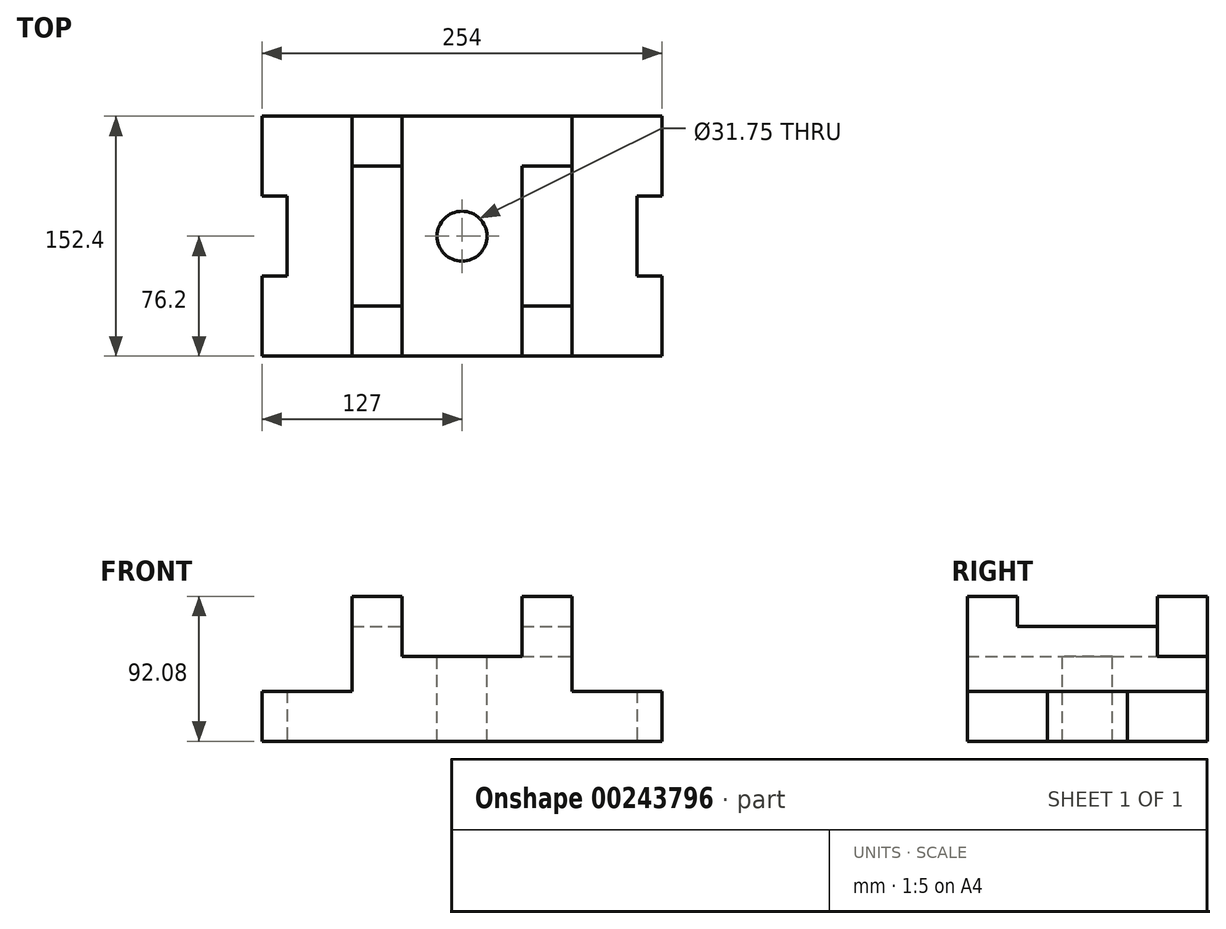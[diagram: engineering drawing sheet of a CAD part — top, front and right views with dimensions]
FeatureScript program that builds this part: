
annotation { "Feature Type Name" : "Feature", "Feature Type Description" : "" }
export const myFeature = defineFeature(function(context is Context, id is Id, definition is map)
    precondition{}
    {
        {
            var Q0;
            Q0=qCreatedBy(makeId("Top.planeOp"),FACE);
            var sketch = newSketch(context, id + "F0", { "sketchPlane" : qUnion([Q0])});
            skLineSegment(sketch, "E0", {"start": v(-127, 152.4) * mm, "end": v(127, 152.4) * mm});
            skLineSegment(sketch, "E1", {"start": v(127, 50.8) * mm, "end": v(127, 0) * mm});
            skLineSegment(sketch, "E2", {"start": v(127, 0) * mm, "end": v(-127, 0) * mm});
            skLineSegment(sketch, "E3", {"start": v(-127, 0) * mm, "end": v(-127, 50.8) * mm});
            skLineSegment(sketch, "E4", {"start": v(-127, 50.8) * mm, "end": v(-111.13, 50.8) * mm});
            skLineSegment(sketch, "E5", {"start": v(-111.13, 50.8) * mm, "end": v(-111.13, 101.6) * mm});
            skLineSegment(sketch, "E6", {"start": v(-111.13, 101.6) * mm, "end": v(-127, 101.6) * mm});
            skLineSegment(sketch, "E7", {"start": v(-127, 101.6) * mm, "end": v(-127, 152.4) * mm});
            skLineSegment(sketch, "E8.MirrorCS", {"start": v(127, 101.6) * mm, "end": v(127, 152.4) * mm});
            skLineSegment(sketch, "E9.MirrorCS", {"start": v(111.12, 101.6) * mm, "end": v(111.12, 50.8) * mm});
            skLineSegment(sketch, "E10", {"start": v(111.12, 101.6) * mm, "end": v(127, 101.6) * mm});
            skLineSegment(sketch, "E11", {"start": v(127, 50.8) * mm, "end": v(111.12, 50.8) * mm});
            skLineSegment(sketch, "E12", {"start": v(0, 0) * mm, "end": v(0, 152.4) * mm, "construction": true});
            skSolve(sketch);
        }
        {
            var Q0;
            Q0=makeQuery(id+"F0.imprint","IMPRINT",FACE,{"disambiguationData":[TD([[makeQuery(id+"F0.imprint","IMPRINT",EDGE,{"derivedFrom":sQuery(id+"F0.wireOp",EDGE,"E0")}),-1.0]])]});
            extrude(context, id + "F1", {"entities" : qUnion([Q0]), "depth" : 31.75 * mm});
        }
        {
            var Q0;
            Q0=makeQuery(id+"F1.opExtrude","CAP_FACE",FACE,{"disambiguationData":[OSD([sQuery(id+"F0.wireOp",EDGE,"E0"),sQuery(id+"F0.wireOp",EDGE,"E1"),sQuery(id+"F0.wireOp",EDGE,"E2"),sQuery(id+"F0.wireOp",EDGE,"E3"),sQuery(id+"F0.wireOp",EDGE,"E4"),sQuery(id+"F0.wireOp",EDGE,"E5"),sQuery(id+"F0.wireOp",EDGE,"E6"),sQuery(id+"F0.wireOp",EDGE,"E7"),sQuery(id+"F0.wireOp",EDGE,"E8.MirrorCS"),sQuery(id+"F0.wireOp",EDGE,"E9.MirrorCS"),sQuery(id+"F0.wireOp",EDGE,"E10"),sQuery(id+"F0.wireOp",EDGE,"E11")])],"isStart":false});
            var sketch = newSketch(context, id + "F2", { "sketchPlane" : qUnion([Q0])});
            skLineSegment(sketch, "E13", {"start": v(-69.85, 152.4) * mm, "end": v(-69.85, 0) * mm});
            skLineSegment(sketch, "E14", {"start": v(-69.85, 0) * mm, "end": v(69.85, 0) * mm});
            skLineSegment(sketch, "E15", {"start": v(69.85, 0) * mm, "end": v(69.85, 152.4) * mm});
            skLineSegment(sketch, "E16", {"start": v(69.85, 152.4) * mm, "end": v(-69.85, 152.4) * mm});
            skSolve(sketch);
        }
        {
            var Q0;
            Q0=makeQuery(id+"F2.imprint","IMPRINT",FACE,{"disambiguationData":[TD([[makeQuery(id+"F2.imprint","IMPRINT",EDGE,{"derivedFrom":sQuery(id+"F2.wireOp",EDGE,"E13")}),1.0]])]});
            extrude(context, id + "F3", {"entities" : qUnion([Q0]), "operationType" : NewBodyOperationType.ADD, "depth" : 22.22 * mm});
        }
        {
            var Q0;
            Q0=makeQuery(id+"F3.opExtrude","CAP_FACE",FACE,{"disambiguationData":[OSD([sQuery(id+"F2.wireOp",EDGE,"E13"),sQuery(id+"F2.wireOp",EDGE,"E14"),sQuery(id+"F2.wireOp",EDGE,"E15"),sQuery(id+"F2.wireOp",EDGE,"E16")])],"isStart":false});
            var sketch = newSketch(context, id + "F4", { "sketchPlane" : qUnion([Q0])});
            skLineSegment(sketch, "E17", {"start": v(-38.1, 152.4) * mm, "end": v(-38.1, 0) * mm});
            skLineSegment(sketch, "E18", {"start": v(-38.1, 0) * mm, "end": v(38.1, 0) * mm});
            skLineSegment(sketch, "E19", {"start": v(38.1, 0) * mm, "end": v(38.1, 152.4) * mm});
            skLineSegment(sketch, "E20", {"start": v(38.1, 152.4) * mm, "end": v(38.1, 120.65) * mm});
            skLineSegment(sketch, "E21", {"start": v(38.1, 120.65) * mm, "end": v(69.85, 120.65) * mm});
            skLineSegment(sketch, "E22", {"start": v(-69.85, 120.65) * mm, "end": v(-38.1, 120.65) * mm});
            skLineSegment(sketch, "E23", {"start": v(-69.85, 31.75) * mm, "end": v(-38.1, 31.75) * mm});
            skLineSegment(sketch, "E24", {"start": v(38.1, 31.75) * mm, "end": v(69.85, 31.75) * mm});
            skSolve(sketch);
        }
        {
            var Q0;
            {var subQ3=sQuery(id+"F4.wireOp",EDGE,"E22");Q0=makeQuery(id+"F4.imprint","IMPRINT",FACE,{"disambiguationData":[TD([[makeQuery(id+"F4.imprint","IMPRINT",EDGE,{"derivedFrom":subQ3}),1.0]])]});}
            var Q1;
            {var subQ3=sQuery(id+"F4.wireOp",EDGE,"E23");Q1=makeQuery(id+"F4.imprint","IMPRINT",FACE,{"disambiguationData":[TD([[makeQuery(id+"F4.imprint","IMPRINT",EDGE,{"derivedFrom":subQ3}),-1.0]])]});}
            var Q2;
            {var subQ3=sQuery(id+"F4.wireOp",EDGE,"E24");Q2=makeQuery(id+"F4.imprint","IMPRINT",FACE,{"disambiguationData":[TD([[makeQuery(id+"F4.imprint","IMPRINT",EDGE,{"derivedFrom":subQ3}),-1.0]])]});}
            var Q3;
            {var subQ0=sQuery(id+"F4.wireOp",EDGE,"E20");Q3=makeQuery(id+"F4.imprint","IMPRINT",FACE,{"disambiguationData":[TD([[makeQuery(id+"F4.imprint","IMPRINT",EDGE,{"derivedFrom":subQ0}),1.0]])]});}
            extrude(context, id + "F5", {"entities" : qUnion([Q0, Q1, Q2, Q3]), "operationType" : NewBodyOperationType.ADD, "depth" : 38.1 * mm});
        }
        {
            var Q0;
            {var subQ0=sQuery(id+"F4.wireOp",EDGE,"E22");Q0=makeQuery(id+"F4.imprint","IMPRINT",FACE,{"disambiguationData":[TD([[makeQuery(id+"F4.imprint","IMPRINT",EDGE,{"derivedFrom":subQ0}),-1.0]])]});}
            var Q1;
            {var subQ0=sQuery(id+"F4.wireOp",EDGE,"E21");Q1=makeQuery(id+"F4.imprint","IMPRINT",FACE,{"disambiguationData":[TD([[makeQuery(id+"F4.imprint","IMPRINT",EDGE,{"derivedFrom":subQ0}),-1.0]])]});}
            extrude(context, id + "F6", {"entities" : qUnion([Q0, Q1]), "operationType" : NewBodyOperationType.ADD, "depth" : 19.05 * mm});
        }
        {
            var Q0;
            {var subQ0=sQuery(id+"F4.wireOp",EDGE,"E18");Q0=makeQuery(id+"F4.imprint","IMPRINT",FACE,{"disambiguationData":[TD([[makeQuery(id+"F4.imprint","IMPRINT",EDGE,{"derivedFrom":subQ0}),-1.0]])]});}
            var sketch = newSketch(context, id + "F7", { "sketchPlane" : qUnion([Q0])});
            skCircle(sketch, "E25", {"center": v(0, 76.2) * mm, "radius": 15.88 * mm});
            skSolve(sketch);
        }
        {
            var Q0;
            Q0 = qSketchRegion(id + "F7", true);
            extrude(context, id + "F8", {"entities" : qUnion([Q0]), "operationType" : NewBodyOperationType.REMOVE, "endBound" : BoundingType.THROUGH_ALL, "oppositeDirection" : true, "depth" : 25.4 * mm});
        }
    });
